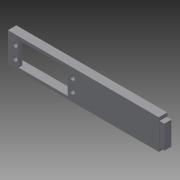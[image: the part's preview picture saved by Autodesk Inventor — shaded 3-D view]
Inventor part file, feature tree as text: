
AUTODESK INVENTOR PART (.ipt)
format: ipt  version: 2015 SP2 (Build 190223200, 223)  size: 148,480 bytes
history: native  units: mm
features: sketch x7, extrude x5, hole x1
ambient origin geometry x8: Origin, YZ Plane, XZ Plane, XY Plane, X Axis, Y Axis, Z Axis, Center Point
bodies: Solid1 (feature_tree)
feature tree (13):
  extrude  "Extrusion1"  Depth=60.0mm
  hole  "Hole1"  [1 undecoded]
  extrude  "Extrusion2"  Depth=4.0mm
  sketch  "Sketch9"  dims[d12=3.0mm d13=3.0mm]
  extrude  "Extrusion3"  Depth=3.0mm
  extrude  "Extrusion4"  Depth=3.0mm
  extrude  "Extrusion5"  Depth=3.0mm
  sketch  "Sketch2"  dims[d2=25.0mm d3=60.0mm]
  sketch  "Sketch4"  dims[d4=3.0mm d5=0.0mm d8=4.0mm]
  sketch  "Sketch8"  dims[d9=4.0mm d11=40.23mm]
  sketch  "Sketch10"  dims[d14=3.0mm d15=3.0mm]
  sketch  "Sketch11"  dims[d16=4.0mm d17=6.0mm d18=4.0mm d19=2.0mm d20=90.0deg d21=8.0mm d22=20.594885mm d23=3.0mm]
  sketch  "Sketch12"  dims[d24=3.0mm d25=3.0mm d26=3.0mm d27=20.0mm d28=3.0mm d29=0.0mm d30=41.0mm d35=4.0mm d36=3.0mm d37=0.0mm d38=0.0mm d39=66.0mm d40=7.0mm d41=0.0mm d42=19.5mm d43=5.9mm d44=4.0mm d45=0.0mm]
note: 1 required parameter value undecoded (feature->parameter linkage not recoverable at this tier; creation-order binding heuristic only, values carry confidence <= 0.55)
